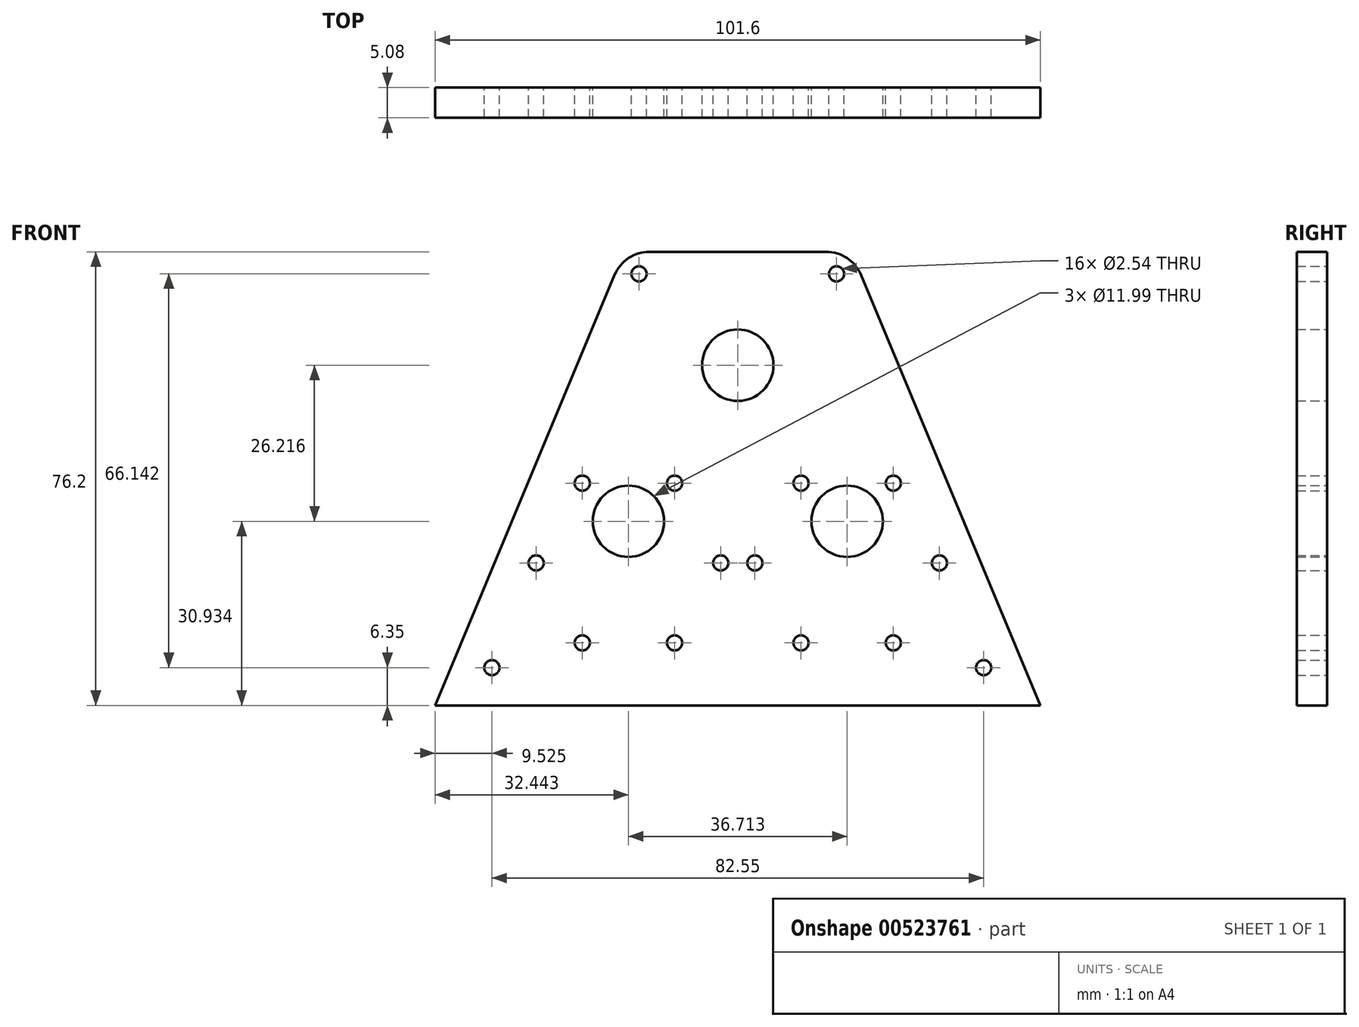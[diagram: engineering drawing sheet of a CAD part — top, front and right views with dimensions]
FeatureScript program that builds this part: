
annotation { "Feature Type Name" : "Feature", "Feature Type Description" : "" }
export const myFeature = defineFeature(function(context is Context, id is Id, definition is map)
    precondition{}
    {
        {
            var Q0;
            Q0=qCreatedBy(makeId("Front.planeOp"),FACE);
            var sketch = newSketch(context, id + "F0", { "sketchPlane" : qUnion([Q0])});
            skLineSegment(sketch, "E0", {"start": v(-9.52, 0) * mm, "end": v(-92.07, 0) * mm});
            skLineSegment(sketch, "E1", {"start": v(-50.8, 76.2) * mm, "end": v(-31.75, 76.2) * mm});
            skLineSegment(sketch, "E2", {"start": v(-35.98, 76.2) * mm, "end": v(-65.62, 76.2) * mm});
            skLineSegment(sketch, "E3", {"start": v(-71.48, 72.3) * mm, "end": v(-97.94, 8.8) * mm});
            skLineSegment(sketch, "E4", {"start": v(-30.12, 72.3) * mm, "end": v(-3.66, 8.8) * mm});
            skPoint(sketch, "E5.visualSharp", {"position": v(0, 0) * mm});
            skPoint(sketch, "E6.visualSharp", {"position": v(-31.75, 76.2) * mm});
            skArc(sketch, "E6.filletArc", {"start": v(-30.12, 72.3) * mm, "mid": v(-32.46, 75.13) * mm, "end": v(-35.98, 76.2) * mm});
            skPoint(sketch, "E7.visualSharp", {"position": v(-69.85, 76.2) * mm});
            skArc(sketch, "E7.filletArc", {"start": v(-65.62, 76.2) * mm, "mid": v(-69.14, 75.13) * mm, "end": v(-71.48, 72.3) * mm});
            skPoint(sketch, "E8.visualSharp", {"position": v(-101.6, 0) * mm});
            skLineSegment(sketch, "E9", {"start": v(-50.8, 76.2) * mm, "end": v(-50.8, 57.15) * mm});
            skCircle(sketch, "E10", {"center": v(-50.8, 57.15) * mm, "radius": 6 * mm});
            skCircle(sketch, "E11", {"center": v(-69.16, 30.93) * mm, "radius": 6 * mm});
            skCircle(sketch, "E12", {"center": v(-32.44, 30.93) * mm, "radius": 6 * mm});
            skCircle(sketch, "E13", {"center": v(-69.16, 23.92) * mm, "radius": 15.5 * mm});
            skLineSegment(sketch, "E14", {"start": v(-69.16, 23.92) * mm, "end": v(-70.64, 21.35) * mm});
            skCircle(sketch, "E15", {"center": v(-76.9, 37.34) * mm, "radius": 1.27 * mm});
            skCircle(sketch, "E16", {"center": v(-84.65, 23.92) * mm, "radius": 1.27 * mm});
            skCircle(sketch, "E17", {"center": v(-76.9, 10.5) * mm, "radius": 1.27 * mm});
            skCircle(sketch, "E18.MirrorC", {"center": v(-61.4, 37.34) * mm, "radius": 1.27 * mm});
            skCircle(sketch, "E19.MirrorC", {"center": v(-53.66, 23.92) * mm, "radius": 1.27 * mm});
            skCircle(sketch, "E20.MirrorC", {"center": v(-61.4, 10.5) * mm, "radius": 1.27 * mm});
            skCircle(sketch, "E21.MirrorC", {"center": v(-47.94, 23.92) * mm, "radius": 1.27 * mm});
            skCircle(sketch, "E22.MirrorC", {"center": v(-40.2, 37.34) * mm, "radius": 1.27 * mm});
            skCircle(sketch, "E23.MirrorC", {"center": v(-40.2, 10.5) * mm, "radius": 1.27 * mm});
            skCircle(sketch, "E24.MirrorC", {"center": v(-24.7, 10.5) * mm, "radius": 1.27 * mm});
            skCircle(sketch, "E25.MirrorC", {"center": v(-16.95, 23.92) * mm, "radius": 1.27 * mm});
            skCircle(sketch, "E26.MirrorC", {"center": v(-24.7, 37.34) * mm, "radius": 1.27 * mm});
            skCircle(sketch, "E27", {"center": v(-9.52, 6.35) * mm, "radius": 1.27 * mm});
            skCircle(sketch, "E28", {"center": v(-92.07, 6.35) * mm, "radius": 1.27 * mm});
            skLineSegment(sketch, "E29", {"start": v(-65.62, 69.85) * mm, "end": v(-69.14, 75.13) * mm});
            skLineSegment(sketch, "E30", {"start": v(-35.98, 69.85) * mm, "end": v(-32.46, 75.13) * mm});
            skLineSegment(sketch, "E31", {"start": v(-65.62, 69.85) * mm, "end": v(-67.38, 72.5) * mm});
            skLineSegment(sketch, "E32", {"start": v(-35.98, 69.85) * mm, "end": v(-34.22, 72.5) * mm});
            skCircle(sketch, "E33", {"center": v(-34.22, 72.5) * mm, "radius": 1.27 * mm});
            skCircle(sketch, "E34", {"center": v(-67.38, 72.5) * mm, "radius": 1.27 * mm});
            skLineSegment(sketch, "E35", {"start": v(-3.66, 8.8) * mm, "end": v(0, 0) * mm});
            skLineSegment(sketch, "E36", {"start": v(-9.52, 0) * mm, "end": v(0, 0) * mm});
            skLineSegment(sketch, "E37", {"start": v(-97.94, 8.8) * mm, "end": v(-101.6, 0) * mm});
            skLineSegment(sketch, "E38", {"start": v(-92.07, 0) * mm, "end": v(-101.6, 0) * mm});
            skSolve(sketch);
        }
        {
            var Q0;
            Q0=makeQuery(id+"F0.imprint","IMPRINT",FACE,{"disambiguationData":[TD([[makeQuery(id+"F0.imprint","IMPRINT",EDGE,{"derivedFrom":sQuery(id+"F0.wireOp",EDGE,"E0")}),-1.0]])]});
            var Q1;
            Q1=makeQuery(id+"F0.imprint","IMPRINT",FACE,{"disambiguationData":[TD([[makeQuery(id+"F0.imprint","IMPRINT",EDGE,{"derivedFrom":sQuery(id+"F0.wireOp",EDGE,"E11")}),-1.0]])]});
            extrude(context, id + "F1", {"entities" : qUnion([Q0, Q1]), "depth" : 5.08 * mm, "offsetDistance" : 25.4 * mm});
        }
    });
